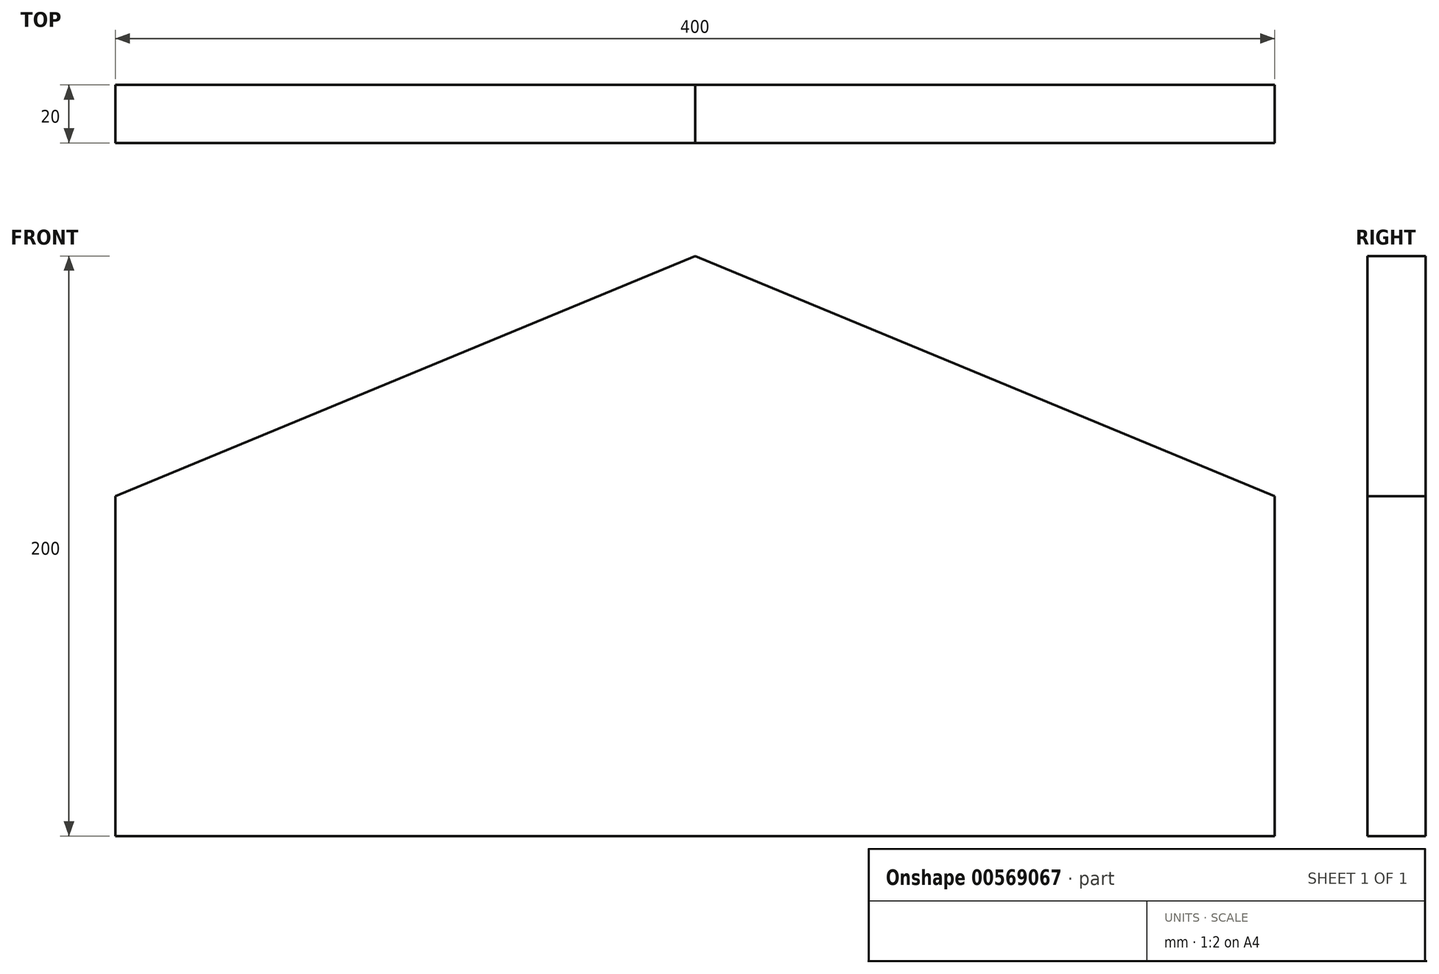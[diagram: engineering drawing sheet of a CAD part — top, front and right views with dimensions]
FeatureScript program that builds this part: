
annotation { "Feature Type Name" : "Feature", "Feature Type Description" : "" }
export const myFeature = defineFeature(function(context is Context, id is Id, definition is map)
    precondition{}
    {
        {
            var Q0;
            Q0=qCreatedBy(makeId("Top.planeOp"),FACE);
            var sketch = newSketch(context, id + "F0", { "sketchPlane" : qUnion([Q0])});
            skLineSegment(sketch, "E0.bottom", {"start": v(-200, 0) * mm, "end": v(200, 0) * mm});
            skLineSegment(sketch, "E0.top", {"start": v(-200, -20) * mm, "end": v(200, -20) * mm});
            skLineSegment(sketch, "E0.left", {"start": v(-200, 0) * mm, "end": v(-200, -20) * mm});
            skLineSegment(sketch, "E0.right", {"start": v(200, 0) * mm, "end": v(200, -20) * mm});
            skSolve(sketch);
        }
        {
            var Q0;
            Q0 = qSketchRegion(id + "F0", true);
            extrude(context, id + "F1", {"entities" : qUnion([Q0]), "depth" : 200 * mm, "offsetDistance" : 25 * mm});
        }
        {
            var Q0;
            Q0=makeQuery(id+"F1.opExtrude","CAP_FACE",FACE,{"disambiguationData":[OSD([sQuery(id+"F0.wireOp",EDGE,"E0.bottom"),sQuery(id+"F0.wireOp",EDGE,"E0.top"),sQuery(id+"F0.wireOp",EDGE,"E0.left"),sQuery(id+"F0.wireOp",EDGE,"E0.right")])],"isStart":false});
            var sketch = newSketch(context, id + "F2", { "sketchPlane" : qUnion([Q0])});
            skLineSegment(sketch, "E1", {"start": v(0, 0) * mm, "end": v(22, 124.76) * mm, "construction": true});
            skLineSegment(sketch, "E2", {"start": v(0, 0) * mm, "end": v(-85.65, -485.74) * mm, "construction": true});
            skLineSegment(sketch, "E3", {"start": v(0, 0) * mm, "end": v(0, -477.96) * mm, "construction": true});
            skSolve(sketch);
        }
        {
            var Q0;
            Q0=makeQuery(id+"F1.opExtrude","SWEPT_FACE",FACE,{"disambiguationData":[OSD([sQuery(id+"F0.wireOp",EDGE,"E0.top")])]});
            var sketch = newSketch(context, id + "F3", { "sketchPlane" : qUnion([Q0])});
            skLineSegment(sketch, "E4", {"start": v(0, 200) * mm, "end": v(-200, 117.16) * mm});
            skLineSegment(sketch, "E5", {"start": v(-200, 117.16) * mm, "end": v(-200, 200) * mm});
            skLineSegment(sketch, "E6", {"start": v(-200, 200) * mm, "end": v(0, 200) * mm});
            skLineSegment(sketch, "E7", {"start": v(0, 200) * mm, "end": v(0, 0) * mm, "construction": true});
            skSolve(sketch);
        }
        {
            var Q0;
            Q0=makeQuery(id+"F3.imprint","IMPRINT",FACE,{"disambiguationData":[TD([[makeQuery(id+"F3.imprint","IMPRINT",EDGE,{"derivedFrom":sQuery(id+"F3.wireOp",EDGE,"E4")}),-1.0]])]});
            extrude(context, id + "F4", {"entities" : qUnion([Q0]), "operationType" : NewBodyOperationType.REMOVE, "endBound" : BoundingType.THROUGH_ALL, "oppositeDirection" : true, "depth" : 25 * mm, "offsetDistance" : 25 * mm});
        }
        {
            var Q0;
            Q0=makeQuery(id+"F1.opExtrude","SWEPT_FACE",FACE,{"disambiguationData":[OSD([sQuery(id+"F0.wireOp",EDGE,"E0.top")])]});
            var sketch = newSketch(context, id + "F5", { "sketchPlane" : qUnion([Q0])});
            skLineSegment(sketch, "E8", {"start": v(0, 200) * mm, "end": v(200, 117.16) * mm});
            skLineSegment(sketch, "E9", {"start": v(200, 117.16) * mm, "end": v(200, 200) * mm});
            skLineSegment(sketch, "E10", {"start": v(200, 200) * mm, "end": v(0, 200) * mm});
            skSolve(sketch);
        }
        {
            var Q0;
            Q0 = qSketchRegion(id + "F5", true);
            extrude(context, id + "F6", {"entities" : qUnion([Q0]), "operationType" : NewBodyOperationType.REMOVE, "endBound" : BoundingType.THROUGH_ALL, "oppositeDirection" : true, "depth" : 25 * mm, "offsetDistance" : 25 * mm});
        }
        {
            var Q0;
            Q0=qCreatedBy(makeId("Top.planeOp"),FACE);
            cPlane(context, id + "F7", {"entities" : qUnion([Q0]), "cplaneType" : CPlaneType.OFFSET, "offset" : 218 * mm, "width" : 150 * mm, "height" : 150 * mm});
        }
        {
            var Q0;
            Q0=qCreatedBy(id+"F7.planeOp",FACE);
            var sketch = newSketch(context, id + "F8", { "sketchPlane" : qUnion([Q0])});
            skLineSegment(sketch, "E11", {"start": v(0, 0) * mm, "end": v(-7.28, -41.3) * mm});
            skLineSegment(sketch, "E12", {"start": v(-7.28, -41.3) * mm, "end": v(252.8, -41.3) * mm});
            skLineSegment(sketch, "E13", {"start": v(252.8, -41.3) * mm, "end": v(252.8, 0) * mm});
            skLineSegment(sketch, "E14", {"start": v(252.8, 0) * mm, "end": v(0, 0) * mm});
            skSolve(sketch);
        }
        {
            var Q0;
            Q0=qCreatedBy(id+"F7.planeOp",FACE);
            var sketch = newSketch(context, id + "F9", { "sketchPlane" : qUnion([Q0])});
            skLineSegment(sketch, "E15", {"start": v(0, 0) * mm, "end": v(-10.9, -61.83) * mm});
            skLineSegment(sketch, "E16", {"start": v(-10.9, -61.83) * mm, "end": v(-240.87, -61.83) * mm});
            skLineSegment(sketch, "E17", {"start": v(-240.87, -61.83) * mm, "end": v(-240.87, 0) * mm});
            skLineSegment(sketch, "E18", {"start": v(-240.87, 0) * mm, "end": v(0, 0) * mm});
            skSolve(sketch);
        }
        {
            var Q0;
            Q0=makeQuery(id+"FLCATjuC7iCxwls_1.boolean.opBoolean","COPY",FACE,{"derivedFrom":makeQuery(id+"FLCATjuC7iCxwls_1.opExtrude","SWEPT_FACE",FACE,{"disambiguationData":[OSD([sQuery(id+"F9.wireOp",EDGE,"E15")])]})});
            var sketch = newSketch(context, id + "F10", { "sketchPlane" : qUnion([Q0])});
            skLineSegment(sketch, "E19", {"start": v(0, 200) * mm, "end": v(20.3, 200) * mm});
            skLineSegment(sketch, "E20", {"start": v(20.3, 198.54) * mm, "end": v(20.3, 200) * mm});
            skLineSegment(sketch, "E21", {"start": v(20.3, 198.54) * mm, "end": v(0, 200) * mm});
            skSolve(sketch);
        }
    });
